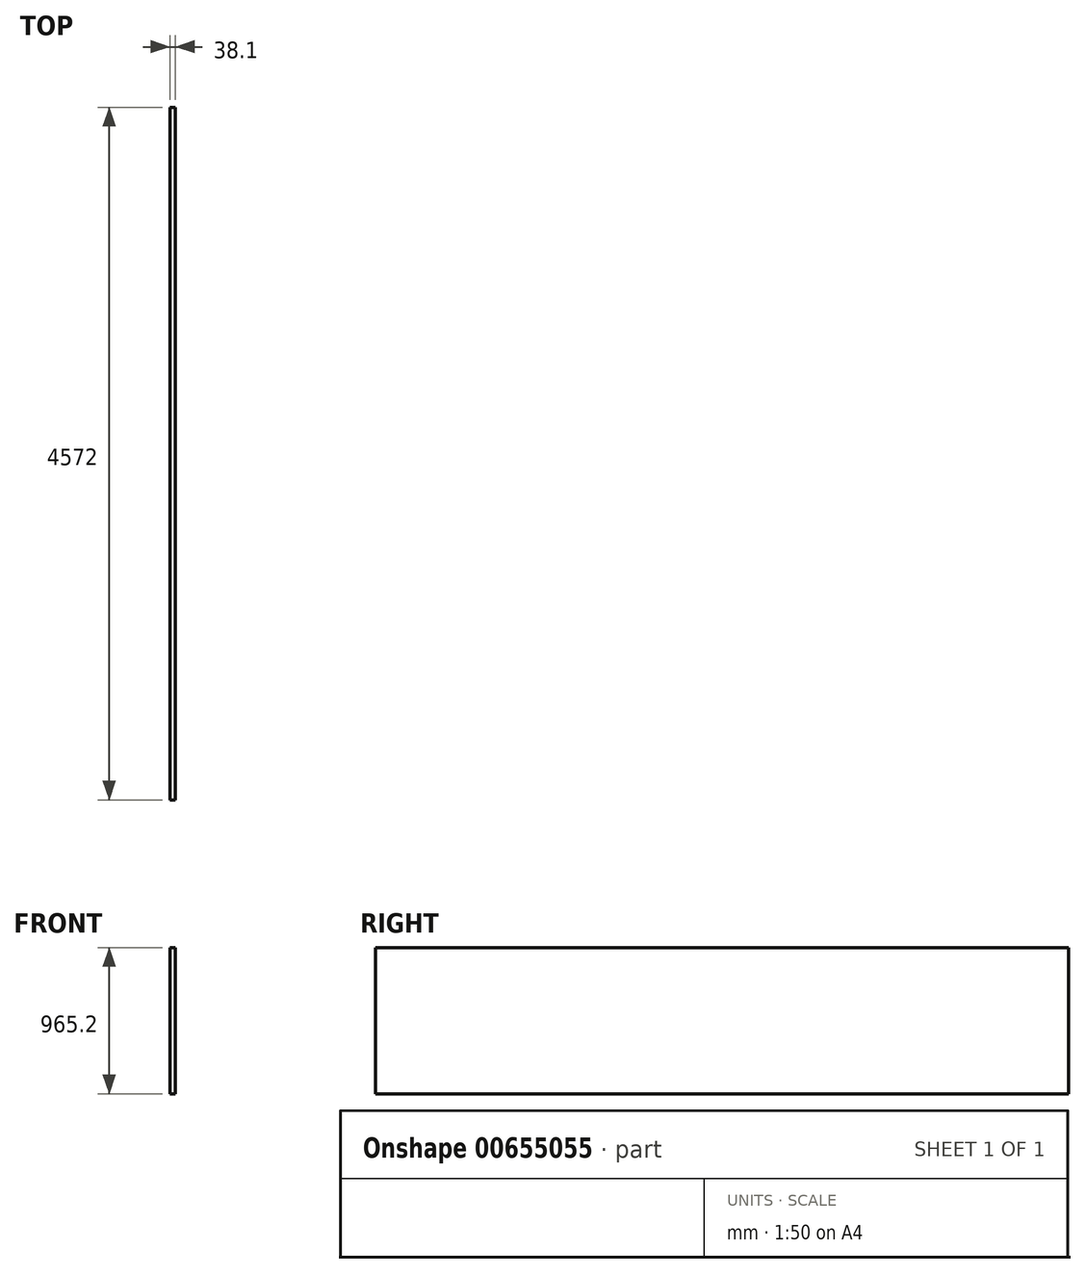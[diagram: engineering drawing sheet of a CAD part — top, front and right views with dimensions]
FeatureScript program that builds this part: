
annotation { "Feature Type Name" : "Feature", "Feature Type Description" : "" }
export const myFeature = defineFeature(function(context is Context, id is Id, definition is map)
    precondition{}
    {
        {
            var Q0;
            Q0=qCreatedBy(makeId("Right.planeOp"),FACE);
            var sketch = newSketch(context, id + "F0", { "sketchPlane" : qUnion([Q0])});
            skLineSegment(sketch, "E0.bottom", {"start": v(0, 0) * mm, "end": v(-4572, 0) * mm});
            skLineSegment(sketch, "E0.top", {"start": v(0, 965.2) * mm, "end": v(-4572, 965.2) * mm});
            skLineSegment(sketch, "E0.left", {"start": v(0, 0) * mm, "end": v(0, 965.2) * mm});
            skLineSegment(sketch, "E0.right", {"start": v(-4572, 0) * mm, "end": v(-4572, 965.2) * mm});
            skSolve(sketch);
        }
        {
            var Q0;
            Q0=makeQuery(id+"F0.imprint","IMPRINT",FACE,{"disambiguationData":[TD([[makeQuery(id+"F0.imprint","IMPRINT",EDGE,{"derivedFrom":sQuery(id+"F0.wireOp",EDGE,"E0.bottom")}),-1.0]])]});
            extrude(context, id + "F1", {"entities" : qUnion([Q0]), "depth" : 38.1 * mm, "offsetDistance" : 25.4 * mm});
        }
    });
